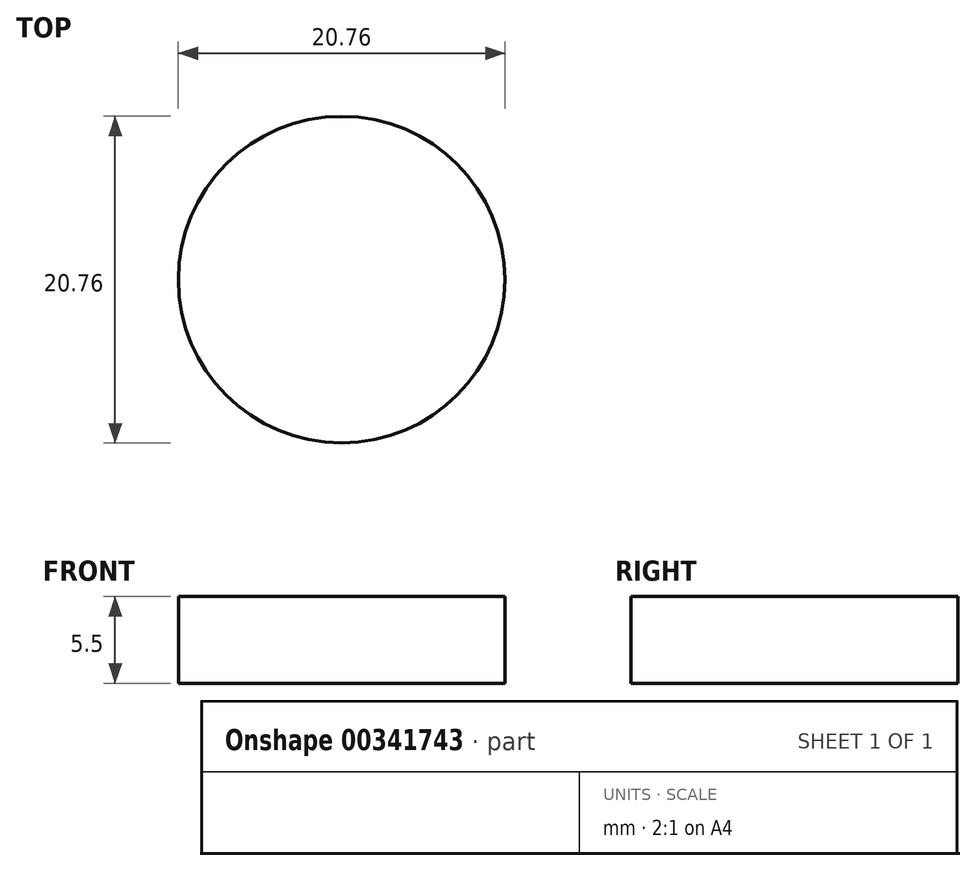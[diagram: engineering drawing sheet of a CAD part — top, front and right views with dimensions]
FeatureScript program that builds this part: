
annotation { "Feature Type Name" : "Feature", "Feature Type Description" : "" }
export const myFeature = defineFeature(function(context is Context, id is Id, definition is map)
    precondition{}
    {
        {
            var Q0;
            Q0=qCreatedBy(makeId("Top.planeOp"),FACE);
            var sketch = newSketch(context, id + "F0", { "sketchPlane" : qUnion([Q0])});
            skCircle(sketch, "E0", {"center": v(0, 0) * mm, "radius": 10.38 * mm});
            skSolve(sketch);
        }
        {
            var Q0;
            Q0=makeQuery(id+"F0.imprint","IMPRINT",FACE,{"disambiguationData":[TD([[makeQuery(id+"F0.imprint","IMPRINT",EDGE,{"derivedFrom":sQuery(id+"F0.wireOp",EDGE,"E0")}),1.0]])]});
            extrude(context, id + "F1", {"entities" : qUnion([Q0]), "depth" : 5.5 * mm});
        }
    });
